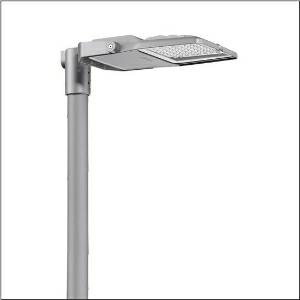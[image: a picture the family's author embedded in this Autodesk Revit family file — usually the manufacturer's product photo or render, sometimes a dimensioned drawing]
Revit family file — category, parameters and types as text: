
# Revit family: floodlight_fl_21_mini___pl43_5xa7776b4a3a_9af8
name_source: partatom
category: Lighting Fixtures
units: mm (PartAtom-declared; Revit-internal decimal feet)

## family parameters
Cut with Voids When Loaded = No
Host = Face
Light Source = No
Part Type = Normal
Room Calculation Point = No
Round Connector Dimension = Use Diameter
Shared = No

## types (1)
- --- (1 x LED, 6650 lm, 45.7 W, 4000K)
    Apparent Load = 46 VA
    CIE Flux Codes = 27 78 99 100 100
    Color Rendering = 70
    Color Temperature = 4000K
    Default Elevation = 1800 mm
    Description = Floodlight FL 21 mini, floodlight, primary light control with lens, of PMMA, primary optical cover: protective disc, of toughened safety glass, transparent, light distribution: PL43, light emission: direct distribution, installation type: surface-mounted, LED, High Power LED, rated luminous flux: 6.650lm, luminous efficacy: 146lm/W, light colour: 740, colour temperature: 4000K, control gear: D4iSmart Interface (Zhaga), control: overheat protection, constant luminous flux control, time-dependent luminous flux control, flexible luminous flux parameterisation, pre-setting: logarithmic dimming characteristic, with terminal, 6-pole, mains connection: 220..240V, AC, 50/60Hz, start of lifetime: 46W, end of service life: 48W, reduction: 22W, mast bracket, of diecast aluminium, powder-coated, Siteco® metallic grey (DB 702S), corrosivity category C5 mid according to DIN EN ISO 12944, suitable for swimming pools, chlorine-resistant, sealing non-destructively replaceable, mast bracket, of steel, galvanised, powder-coated, Siteco® metallic grey (DB 702S), Smart Interface below and above, protection rating (complete): IP66, insulation class (complete): insulation class II (safety insulation), certification: CE, ENEC, VDE, protection symbol: D, impact resistance: IK08, permissible operating ambient temperature: -40..+40°C, permissible operating ambient temperature for outdoor applications: -40..+50°C, standard: DIN EN 12944, LABS conformity tested according to VDMA 24364:2018-05, packaging unit: 1 piece

Light Distribution: PL43
    Height = 70 mm
    Lamp = 1 x LED
    Lamp Light Flux = 6650 lm
    Lamp Power = 45.7 W
    Lamp count = 1
    Length = 485 mm
    Luminous efficacy = 146 lm/W
    Manufacturer = Siteco
    ModVariant = No
    Model = 5XA7776B4A3A
    Number of Poles = 1
    OnlyDefault = Yes
    Power Factor = 1
    Product Name = Floodlight FL 21 mini | PL43
    Product group = floodlight | pylon annexe
    ProductGroupID = 6200
    Protection Class = Protection class II
    Protection Degree = IP 66
    RLX_Detail_Level = 1
    RLX_Emergency_Light_Flux = 0 lm
    RLX_Emergency_Type = 0
    RLX_Emergency_Type_DB = No
    RlxData = <blob elided: 101101 chars, md5=9c21e071>
    Socket = socket
    Standby Power = 0 W
    System Light Flux = 6650 lm
    System Power = 46 W
    Type Comments = factory setting: luminous flux: 100 % | dim-lin: 254 | 463 mA
    Type Image = l_1007125.jpg
    URL = http://relux.com
    VarID = @adj_095268
    Voltage = 0 V
    Weight = 0.00 kg
    Width = 337 mm

## geometry (parser evidence)
native form markers: Blend x4, Sweep x14
no freeform markers — native parametric forms only
